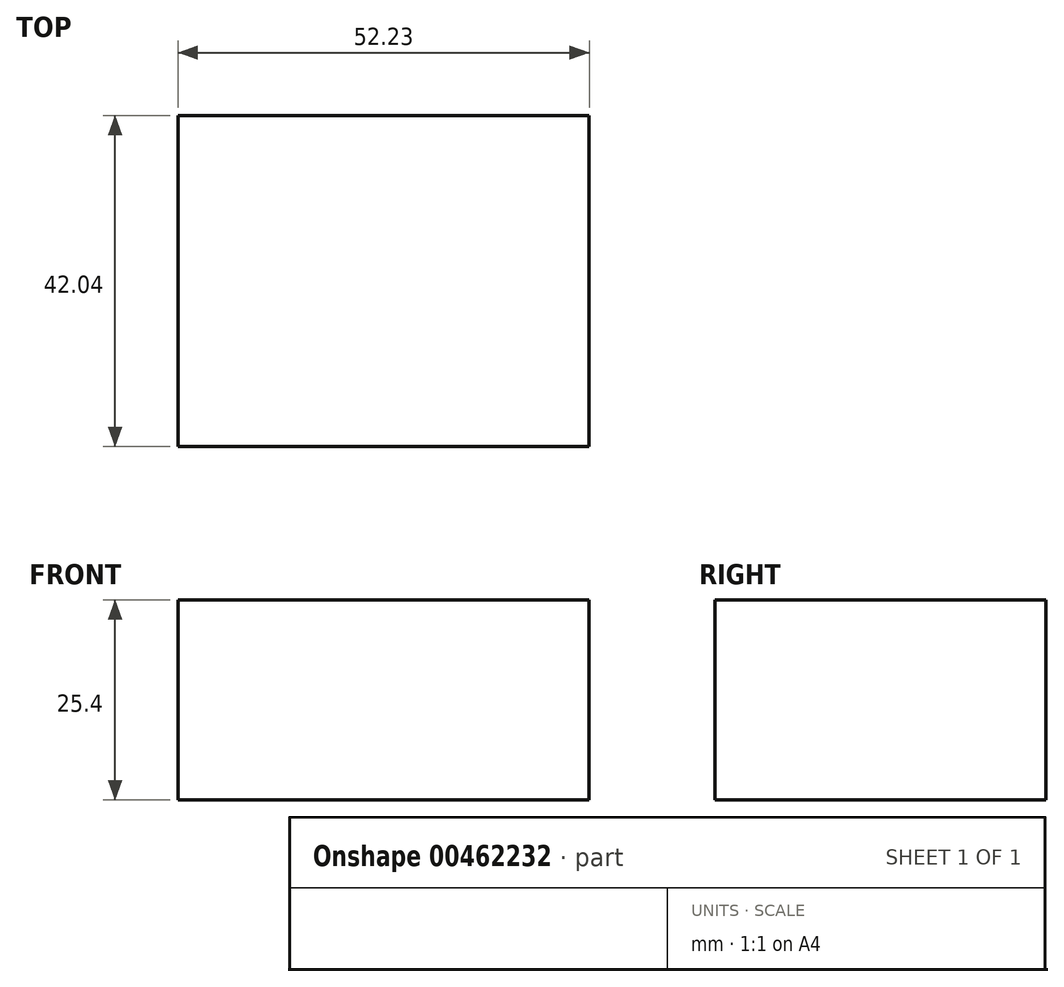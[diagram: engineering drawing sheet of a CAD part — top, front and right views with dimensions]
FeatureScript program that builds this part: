
annotation { "Feature Type Name" : "Feature", "Feature Type Description" : "" }
export const myFeature = defineFeature(function(context is Context, id is Id, definition is map)
    precondition{}
    {
        {
            var Q0;
            Q0=qCreatedBy(makeId("Top.planeOp"),FACE);
            var sketch = newSketch(context, id + "F0", { "sketchPlane" : qUnion([Q0])});
            skLineSegment(sketch, "E0", {"start": v(0, 0) * mm, "end": v(0, 42.04) * mm});
            skLineSegment(sketch, "E1", {"start": v(0, 42.04) * mm, "end": v(52.23, 42.04) * mm});
            skLineSegment(sketch, "E2", {"start": v(52.23, 42.04) * mm, "end": v(52.23, 0) * mm});
            skLineSegment(sketch, "E3", {"start": v(52.23, 0) * mm, "end": v(0, 0) * mm});
            skSolve(sketch);
        }
        {
            var Q0;
            Q0 = qSketchRegion(id + "F0", true);
            extrude(context, id + "F1", {"entities" : qUnion([Q0]), "depth" : 25.4 * mm});
        }
    });
